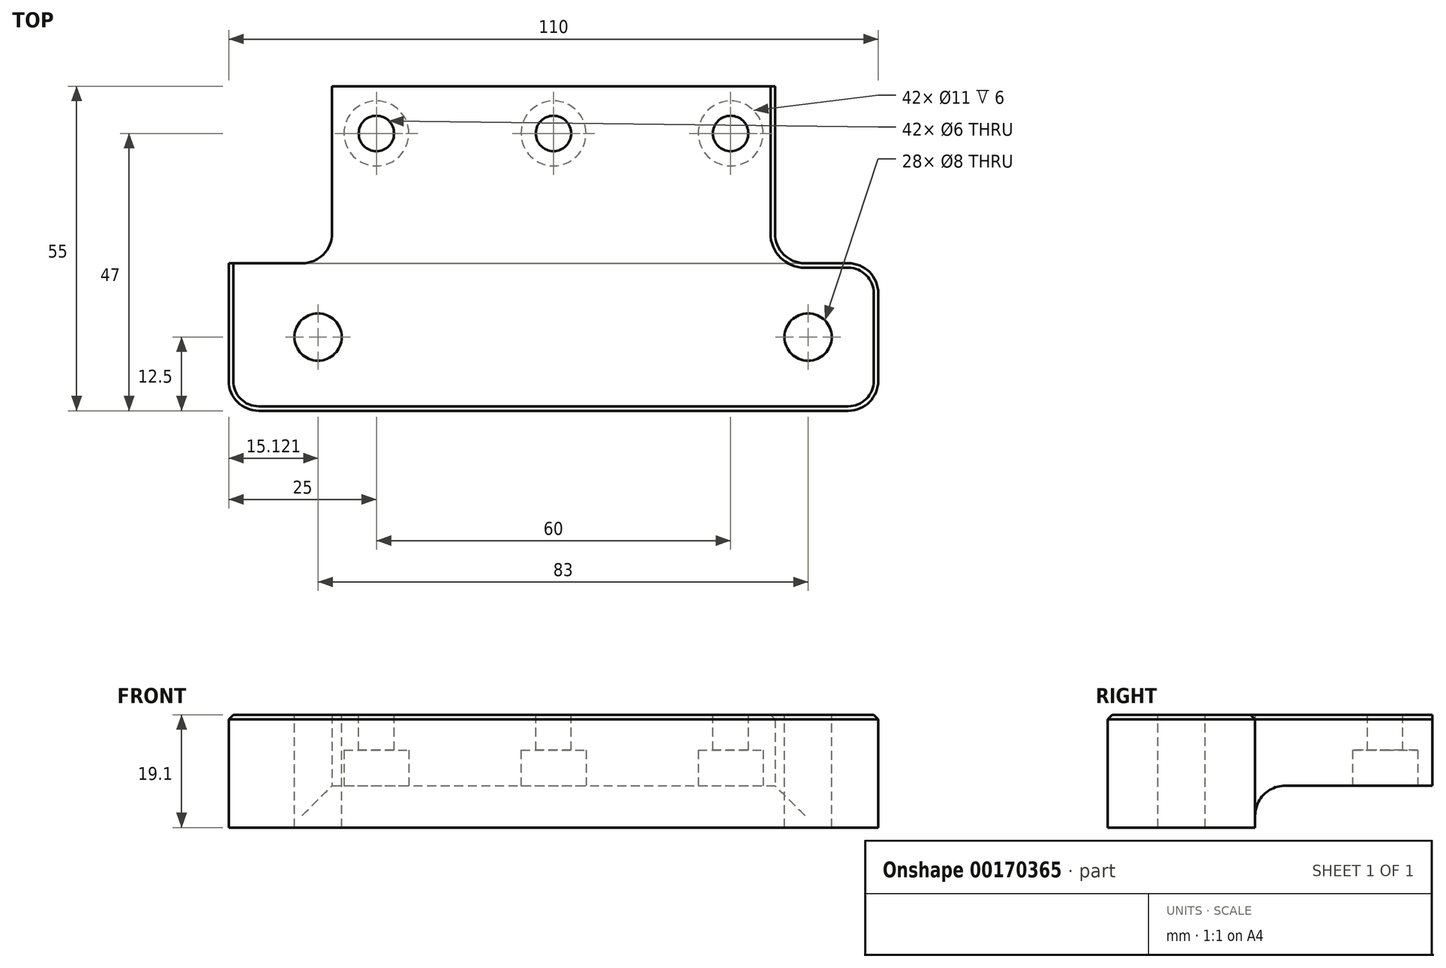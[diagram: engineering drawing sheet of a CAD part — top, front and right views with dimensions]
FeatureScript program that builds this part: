
annotation { "Feature Type Name" : "Feature", "Feature Type Description" : "" }
export const myFeature = defineFeature(function(context is Context, id is Id, definition is map)
    precondition{}
    {
        {
            var Q0;
            Q0=qCreatedBy(makeId("Top.planeOp"),FACE);
            var sketch = newSketch(context, id + "F0", { "sketchPlane" : qUnion([Q0])});
            skPoint(sketch, "E0.middle", {"position": v(0, 0) * mm});
            skLineSegment(sketch, "E1", {"start": v(-55, -27.5) * mm, "end": v(-55, -2.5) * mm});
            skLineSegment(sketch, "E2", {"start": v(-55, -2.5) * mm, "end": v(-37.5, -2.5) * mm});
            skLineSegment(sketch, "E3", {"start": v(-37.5, -2.5) * mm, "end": v(-37.5, 27.5) * mm});
            skLineSegment(sketch, "E4.MirrorCS", {"start": v(37.5, -2.5) * mm, "end": v(37.5, 27.5) * mm});
            skLineSegment(sketch, "E5.MirrorCS", {"start": v(55, -27.5) * mm, "end": v(55, -2.5) * mm});
            skLineSegment(sketch, "E6.MirrorCS", {"start": v(55, -2.5) * mm, "end": v(37.5, -2.5) * mm});
            skLineSegment(sketch, "E7", {"start": v(-55, -27.5) * mm, "end": v(55, -27.5) * mm});
            skLineSegment(sketch, "E8", {"start": v(-37.5, 27.5) * mm, "end": v(37.5, 27.5) * mm});
            skSolve(sketch);
        }
        {
            var Q0;
            Q0=makeQuery(id+"F0.imprint","IMPRINT",FACE,{"disambiguationData":[TD([[makeQuery(id+"F0.imprint","IMPRINT",EDGE,{"derivedFrom":sQuery(id+"F0.wireOp",EDGE,"E1")}),-1.0]])]});
            extrude(context, id + "F1", {"entities" : qUnion([Q0]), "depth" : 19.1 * mm});
        }
        {
            var Q0;
            Q0=makeQuery(id+"F1.opExtrude","CAP_FACE",FACE,{"disambiguationData":[OSD([sQuery(id+"F0.wireOp",EDGE,"E1"),sQuery(id+"F0.wireOp",EDGE,"E2"),sQuery(id+"F0.wireOp",EDGE,"E3"),sQuery(id+"F0.wireOp",EDGE,"E4.MirrorCS"),sQuery(id+"F0.wireOp",EDGE,"E5.MirrorCS"),sQuery(id+"F0.wireOp",EDGE,"E6.MirrorCS"),sQuery(id+"F0.wireOp",EDGE,"E7"),sQuery(id+"F0.wireOp",EDGE,"E8")])],"isStart":false});
            var sketch = newSketch(context, id + "F2", { "sketchPlane" : qUnion([Q0])});
            skCircle(sketch, "E9", {"center": v(-30, 19.5) * mm, "radius": 3 * mm});
            skCircle(sketch, "E10", {"center": v(30, 19.5) * mm, "radius": 3 * mm});
            skCircle(sketch, "E11", {"center": v(0, 19.5) * mm, "radius": 3 * mm});
            skSolve(sketch);
        }
        {
            var Q0;
            Q0=makeQuery(id+"F2.imprint","IMPRINT",FACE,{"disambiguationData":[TD([[makeQuery(id+"F2.imprint","IMPRINT",EDGE,{"derivedFrom":sQuery(id+"F2.wireOp",EDGE,"E9")}),1.0]])]});
            var Q1;
            Q1=makeQuery(id+"F2.imprint","IMPRINT",FACE,{"disambiguationData":[TD([[makeQuery(id+"F2.imprint","IMPRINT",EDGE,{"derivedFrom":sQuery(id+"F2.wireOp",EDGE,"E11")}),1.0]])]});
            var Q2;
            Q2=makeQuery(id+"F2.imprint","IMPRINT",FACE,{"disambiguationData":[TD([[makeQuery(id+"F2.imprint","IMPRINT",EDGE,{"derivedFrom":sQuery(id+"F2.wireOp",EDGE,"E10")}),1.0]])]});
            extrude(context, id + "F3", {"entities" : qUnion([Q0, Q1, Q2]), "operationType" : NewBodyOperationType.REMOVE, "endBound" : BoundingType.THROUGH_ALL, "oppositeDirection" : true, "depth" : 25.4 * mm});
        }
        {
            var Q0;
            Q0=makeQuery(id+"F1.opExtrude","CAP_FACE",FACE,{"disambiguationData":[OSD([sQuery(id+"F0.wireOp",EDGE,"E1"),sQuery(id+"F0.wireOp",EDGE,"E2"),sQuery(id+"F0.wireOp",EDGE,"E3"),sQuery(id+"F0.wireOp",EDGE,"E4.MirrorCS"),sQuery(id+"F0.wireOp",EDGE,"E5.MirrorCS"),sQuery(id+"F0.wireOp",EDGE,"E6.MirrorCS"),sQuery(id+"F0.wireOp",EDGE,"E7"),sQuery(id+"F0.wireOp",EDGE,"E8")])],"isStart":true});
            var sketch = newSketch(context, id + "F4", { "sketchPlane" : qUnion([Q0])});
            skCircle(sketch, "E12", {"center": v(-30, -19.5) * mm, "radius": 5.5 * mm});
            skCircle(sketch, "E13", {"center": v(0, -19.5) * mm, "radius": 5.5 * mm});
            skCircle(sketch, "E14", {"center": v(30, -19.5) * mm, "radius": 5.5 * mm});
            skSolve(sketch);
        }
        {
            var Q0;
            Q0=makeQuery(id+"F4.imprint","IMPRINT",FACE,{"disambiguationData":[TD([[makeQuery(id+"F4.imprint","IMPRINT",EDGE,{"derivedFrom":sQuery(id+"F4.wireOp",EDGE,"E12")}),1.0]])]});
            var Q1;
            Q1=makeQuery(id+"F4.imprint","IMPRINT",FACE,{"disambiguationData":[TD([[makeQuery(id+"F4.imprint","IMPRINT",EDGE,{"derivedFrom":sQuery(id+"F4.wireOp",EDGE,"E13")}),1.0]])]});
            var Q2;
            Q2=makeQuery(id+"F4.imprint","IMPRINT",FACE,{"disambiguationData":[TD([[makeQuery(id+"F4.imprint","IMPRINT",EDGE,{"derivedFrom":sQuery(id+"F4.wireOp",EDGE,"E14")}),1.0]])]});
            var Q3;
            Q3=sQuery(id+"F4.wireOp",EDGE,"E12");
            var Q4;
            Q4=sQuery(id+"F4.wireOp",EDGE,"E13");
            var Q5;
            Q5=sQuery(id+"F4.wireOp",EDGE,"E14");
            extrude(context, id + "F5", {"entities" : qUnion([Q0, Q1, Q2]), "operationType" : NewBodyOperationType.REMOVE, "surfaceEntities" : qUnion([Q3, Q4, Q5]), "oppositeDirection" : true, "depth" : 13.1 * mm});
        }
        {
            var Q0;
            Q0=makeQuery(id+"F1.opExtrude","SWEPT_FACE",FACE,{"disambiguationData":[OSD([sQuery(id+"F0.wireOp",EDGE,"E4.MirrorCS")])]});
            var sketch = newSketch(context, id + "F6", { "sketchPlane" : qUnion([Q0])});
            skLineSegment(sketch, "E15", {"start": v(14.26, 7.1) * mm, "end": v(27.5, 7.1) * mm});
            skLineSegment(sketch, "E16", {"start": v(27.5, 7.1) * mm, "end": v(-2.5, 7.1) * mm});
            skLineSegment(sketch, "E17", {"start": v(-2.5, 7.1) * mm, "end": v(-2.5, 0) * mm});
            skLineSegment(sketch, "E18", {"start": v(-2.5, 0) * mm, "end": v(27.5, 0) * mm});
            skLineSegment(sketch, "E19", {"start": v(27.5, 0) * mm, "end": v(27.5, 7.1) * mm});
            skSolve(sketch);
        }
        {
            var Q0;
            {var subQ0=sQuery(id+"F6.wireOp",EDGE,"E17");Q0=makeQuery(id+"F6.imprint","IMPRINT",FACE,{"disambiguationData":[TD([[makeQuery(id+"F6.imprint","IMPRINT",EDGE,{"derivedFrom":subQ0}),1.0]])]});}
            extrude(context, id + "F7", {"entities" : qUnion([Q0]), "operationType" : NewBodyOperationType.REMOVE, "endBound" : BoundingType.THROUGH_ALL, "oppositeDirection" : true, "depth" : 25.4 * mm});
        }
        {
            var Q0;
            Q0=makeQuery(id+"F1.opExtrude","CAP_FACE",FACE,{"disambiguationData":[OSD([sQuery(id+"F0.wireOp",EDGE,"E1"),sQuery(id+"F0.wireOp",EDGE,"E2"),sQuery(id+"F0.wireOp",EDGE,"E3"),sQuery(id+"F0.wireOp",EDGE,"E4.MirrorCS"),sQuery(id+"F0.wireOp",EDGE,"E5.MirrorCS"),sQuery(id+"F0.wireOp",EDGE,"E6.MirrorCS"),sQuery(id+"F0.wireOp",EDGE,"E7"),sQuery(id+"F0.wireOp",EDGE,"E8")])],"isStart":false});
            var sketch = newSketch(context, id + "F8", { "sketchPlane" : qUnion([Q0])});
            skCircle(sketch, "E20", {"center": v(-39.88, -15) * mm, "radius": 4 * mm});
            skCircle(sketch, "E21", {"center": v(43.12, -15) * mm, "radius": 4 * mm});
            skSolve(sketch);
        }
        {
            var Q0;
            Q0=makeQuery(id+"F8.imprint","IMPRINT",FACE,{"disambiguationData":[TD([[makeQuery(id+"F8.imprint","IMPRINT",EDGE,{"derivedFrom":sQuery(id+"F8.wireOp",EDGE,"E20")}),1.0]])]});
            var Q1;
            Q1=makeQuery(id+"F8.imprint","IMPRINT",FACE,{"disambiguationData":[TD([[makeQuery(id+"F8.imprint","IMPRINT",EDGE,{"derivedFrom":sQuery(id+"F8.wireOp",EDGE,"E21")}),1.0]])]});
            extrude(context, id + "F9", {"entities" : qUnion([Q0, Q1]), "operationType" : NewBodyOperationType.REMOVE, "endBound" : BoundingType.THROUGH_ALL, "oppositeDirection" : true, "depth" : 25.4 * mm});
        }
        {
            var Q0;
            Q0=makeQuery(id+"F1.opExtrude","SWEPT_EDGE",EDGE,{"disambiguationData":[OSD([sQuery(id+"F0.wireOp",EDGE,"E5.MirrorCS"),sQuery(id+"F0.wireOp",EDGE,"E6.MirrorCS")])]});
            var Q1;
            Q1=makeQuery(id+"F1.opExtrude","SWEPT_EDGE",EDGE,{"disambiguationData":[OSD([sQuery(id+"F0.wireOp",EDGE,"E4.MirrorCS"),sQuery(id+"F0.wireOp",EDGE,"E6.MirrorCS")])]});
            var Q2;
            Q2=makeQuery(id+"F1.opExtrude","SWEPT_EDGE",EDGE,{"disambiguationData":[OSD([sQuery(id+"F0.wireOp",EDGE,"E2"),sQuery(id+"F0.wireOp",EDGE,"E3")])]});
            var Q3;
            Q3=makeQuery(id+"F1.opExtrude","SWEPT_EDGE",EDGE,{"disambiguationData":[OSD([sQuery(id+"F0.wireOp",EDGE,"E1"),sQuery(id+"F0.wireOp",EDGE,"E2")])]});
            var Q4;
            Q4=makeQuery(id+"F1.opExtrude","SWEPT_EDGE",EDGE,{"disambiguationData":[OSD([sQuery(id+"F0.wireOp",EDGE,"E5.MirrorCS"),sQuery(id+"F0.wireOp",EDGE,"E7")])]});
            var Q5;
            Q5=makeQuery(id+"F1.opExtrude","SWEPT_EDGE",EDGE,{"disambiguationData":[OSD([sQuery(id+"F0.wireOp",EDGE,"E1"),sQuery(id+"F0.wireOp",EDGE,"E7")])]});
            fillet(context, id + "F10", {"entities" : qUnion([Q0, Q1, Q2, Q3, Q4, Q5]), "radius" : 5.08 * mm, "tangentPropagation" : true, "allowEdgeOverflow" : false});
        }
        {
            var Q0;
            Q0=makeQuery(id+"F7.boolean.opBoolean","COPY",EDGE,{"derivedFrom":makeQuery(id+"F7.opExtrude","SWEPT_EDGE",EDGE,{"disambiguationData":[OSD([sQuery(id+"F0.wireOp",EDGE,"E4.MirrorCS"),sQuery(id+"F0.wireOp",EDGE,"E6.MirrorCS"),sQuery(id+"F6.wireOp",EDGE,"E16"),sQuery(id+"F6.wireOp",EDGE,"E17")])]})});
            fillet(context, id + "F11", {"entities" : qUnion([Q0]), "radius" : 5.08 * mm, "tangentPropagation" : true, "allowEdgeOverflow" : false});
        }
        {
            var Q0;
            Q0=makeQuery(id+"F1.opExtrude","CAP_EDGE",EDGE,{"disambiguationData":[OSD([sQuery(id+"F0.wireOp",EDGE,"E7")])],"isStart":false});
            chamfer(context, id + "F12", {"entities" : qUnion([Q0]), "width" : 0.76 * mm, "tangentPropagation" : true});
        }
    });
